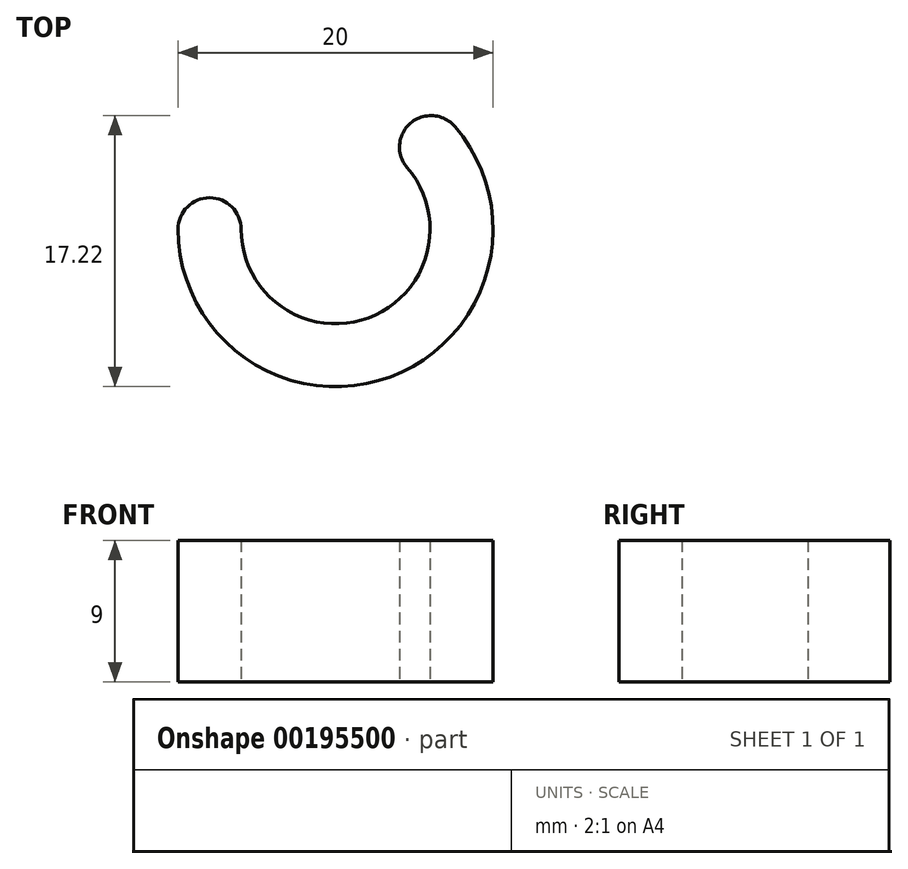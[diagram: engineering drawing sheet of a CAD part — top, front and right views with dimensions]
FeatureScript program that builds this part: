
annotation { "Feature Type Name" : "Feature", "Feature Type Description" : "" }
export const myFeature = defineFeature(function(context is Context, id is Id, definition is map)
    precondition{}
    {
        {
            var Q0;
            Q0=qCreatedBy(makeId("Top.planeOp"),FACE);
            var sketch = newSketch(context, id + "F0", { "sketchPlane" : qUnion([Q0])});
            skArc(sketch, "E0", {"start": v(-6, 0) * mm, "mid": v(2.09, -5.63) * mm, "end": v(4.55, 3.91) * mm});
            skArc(sketch, "E1", {"start": v(-10, 0) * mm, "mid": v(3.48, -9.38) * mm, "end": v(7.58, 6.52) * mm});
            skCircle(sketch, "E2", {"center": v(-8, 0) * mm, "radius": 2 * mm});
            skCircle(sketch, "E3", {"center": v(6.06, 5.22) * mm, "radius": 2 * mm});
            skSolve(sketch);
        }
        {
            var Q0;
            Q0 = qSketchRegion(id + "F0", true);
            extrude(context, id + "F1", {"entities" : qUnion([Q0]), "depth" : 9 * mm});
        }
    });
